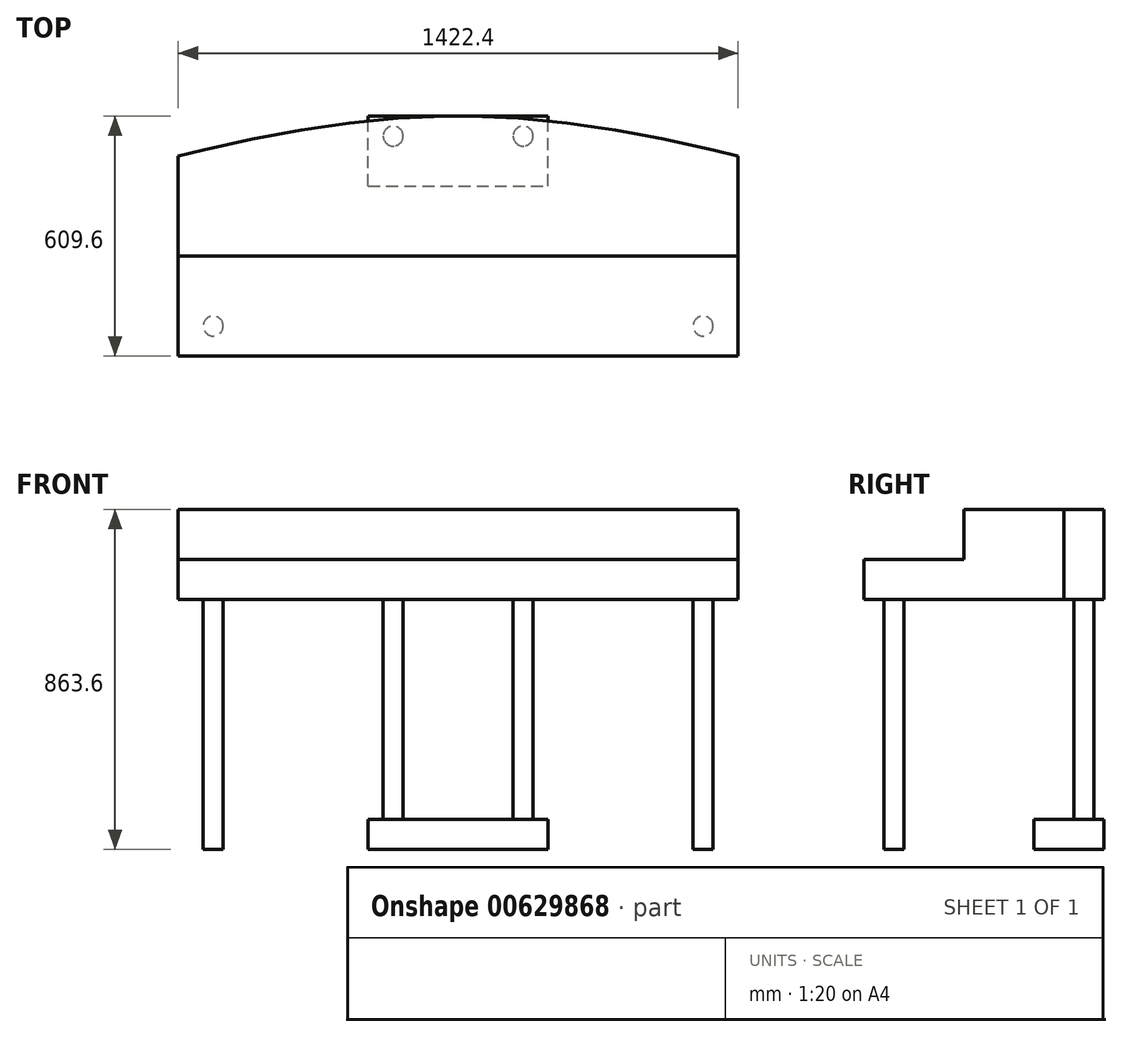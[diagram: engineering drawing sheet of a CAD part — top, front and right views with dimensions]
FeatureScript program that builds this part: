
annotation { "Feature Type Name" : "Feature", "Feature Type Description" : "" }
export const myFeature = defineFeature(function(context is Context, id is Id, definition is map)
    precondition{}
    {
        {
            var Q0;
            Q0=qCreatedBy(makeId("Top.planeOp"),FACE);
            var sketch = newSketch(context, id + "F0", { "sketchPlane" : qUnion([Q0])});
            skLineSegment(sketch, "E0.bottom", {"start": v(0, 0) * mm, "end": v(1422.4, 0) * mm});
            skLineSegment(sketch, "E0.left", {"start": v(0, 0) * mm, "end": v(0, 508) * mm});
            skLineSegment(sketch, "E0.right", {"start": v(1422.4, 0) * mm, "end": v(1422.4, 508) * mm});
            skFitSpline(sketch, "E1", {"points": [v(0, 508) * mm, v(711.2, 609.6) * mm, v(1422.4, 508) * mm], "startDerivative": vector(1449.3, 359.1) * mm, "endDerivative": vector(1449.3, -359.1) * mm});
            skLineSegment(sketch, "E2", {"start": v(711.2, 0) * mm, "end": v(711.2, 609.6) * mm, "construction": true});
            skLineSegment(sketch, "E3", {"start": v(0, 254) * mm, "end": v(1422.4, 254) * mm});
            skCircle(sketch, "E4", {"center": v(546.1, 558.8) * mm, "radius": 25.4 * mm});
            skCircle(sketch, "E5", {"center": v(876.3, 558.8) * mm, "radius": 25.4 * mm});
            skCircle(sketch, "E6", {"center": v(1333.5, 76.2) * mm, "radius": 25.4 * mm});
            skCircle(sketch, "E7", {"center": v(88.9, 76.2) * mm, "radius": 25.4 * mm});
            skSolve(sketch);
        }
        {
            var Q0;
            {var subQ1=sQuery(id+"F0.wireOp",EDGE,"E1");Q0=makeQuery(id+"F0.imprint","IMPRINT",FACE,{"disambiguationData":[TD([[makeQuery(id+"F0.imprint","IMPRINT",EDGE,{"derivedFrom":subQ1}),-1.0]])]});}
            var Q1;
            Q1=makeQuery(id+"F0.imprint","IMPRINT",FACE,{"disambiguationData":[TD([[makeQuery(id+"F0.imprint","IMPRINT",EDGE,{"derivedFrom":sQuery(id+"F0.wireOp",EDGE,"E4")}),1.0]])]});
            var Q2;
            Q2=makeQuery(id+"F0.imprint","IMPRINT",FACE,{"disambiguationData":[TD([[makeQuery(id+"F0.imprint","IMPRINT",EDGE,{"derivedFrom":sQuery(id+"F0.wireOp",EDGE,"E5")}),1.0]])]});
            extrude(context, id + "F1", {"entities" : qUnion([Q0, Q1, Q2]), "depth" : 228.6 * mm, "offsetDistance" : 25.4 * mm});
        }
        {
            var Q0;
            {var subQ1=sQuery(id+"F0.wireOp",EDGE,"E0.bottom");Q0=makeQuery(id+"F0.imprint","IMPRINT",FACE,{"disambiguationData":[TD([[makeQuery(id+"F0.imprint","IMPRINT",EDGE,{"derivedFrom":subQ1}),1.0]])]});}
            var Q1;
            Q1=makeQuery(id+"F0.imprint","IMPRINT",FACE,{"disambiguationData":[TD([[makeQuery(id+"F0.imprint","IMPRINT",EDGE,{"derivedFrom":sQuery(id+"F0.wireOp",EDGE,"E7")}),1.0]])]});
            var Q2;
            Q2=makeQuery(id+"F0.imprint","IMPRINT",FACE,{"disambiguationData":[TD([[makeQuery(id+"F0.imprint","IMPRINT",EDGE,{"derivedFrom":sQuery(id+"F0.wireOp",EDGE,"E6")}),1.0]])]});
            extrude(context, id + "F2", {"entities" : qUnion([Q0, Q1, Q2]), "operationType" : NewBodyOperationType.ADD, "depth" : 101.6 * mm, "offsetDistance" : 25.4 * mm});
        }
        {
            var Q0;
            Q0=makeQuery(id+"F0.imprint","IMPRINT",FACE,{"disambiguationData":[TD([[makeQuery(id+"F0.imprint","IMPRINT",EDGE,{"derivedFrom":sQuery(id+"F0.wireOp",EDGE,"E5")}),1.0]])]});
            var Q1;
            Q1=makeQuery(id+"F0.imprint","IMPRINT",FACE,{"disambiguationData":[TD([[makeQuery(id+"F0.imprint","IMPRINT",EDGE,{"derivedFrom":sQuery(id+"F0.wireOp",EDGE,"E4")}),1.0]])]});
            var Q2;
            Q2=makeQuery(id+"F0.imprint","IMPRINT",FACE,{"disambiguationData":[TD([[makeQuery(id+"F0.imprint","IMPRINT",EDGE,{"derivedFrom":sQuery(id+"F0.wireOp",EDGE,"E6")}),1.0]])]});
            var Q3;
            Q3=makeQuery(id+"F0.imprint","IMPRINT",FACE,{"disambiguationData":[TD([[makeQuery(id+"F0.imprint","IMPRINT",EDGE,{"derivedFrom":sQuery(id+"F0.wireOp",EDGE,"E7")}),1.0]])]});
            var Q4;
            Q4=sQuery(id+"F0.wireOp",EDGE,"E5");
            var Q5;
            Q5=sQuery(id+"F0.wireOp",EDGE,"E4");
            var Q6;
            Q6=sQuery(id+"F0.wireOp",EDGE,"E6");
            var Q7;
            Q7=sQuery(id+"F0.wireOp",EDGE,"E7");
            extrude(context, id + "F3", {"entities" : qUnion([Q0, Q1, Q2, Q3]), "operationType" : NewBodyOperationType.ADD, "surfaceEntities" : qUnion([Q4, Q5, Q6, Q7]), "oppositeDirection" : true, "depth" : 635 * mm, "offsetDistance" : 25.4 * mm});
        }
        {
            var Q0;
            Q0=makeQuery(id+"F3.opExtrude","CAP_FACE",FACE,{"disambiguationData":[OSD([sQuery(id+"F0.wireOp",EDGE,"E4")])],"isStart":false});
            var sketch = newSketch(context, id + "F4", { "sketchPlane" : qUnion([Q0])});
            skLineSegment(sketch, "E8.bottom", {"start": v(482.6, -431.8) * mm, "end": v(939.8, -431.8) * mm});
            skLineSegment(sketch, "E8.top", {"start": v(482.6, -609.6) * mm, "end": v(939.8, -609.6) * mm});
            skLineSegment(sketch, "E8.left", {"start": v(482.6, -431.8) * mm, "end": v(482.6, -609.6) * mm});
            skLineSegment(sketch, "E8.right", {"start": v(939.8, -431.8) * mm, "end": v(939.8, -609.6) * mm});
            skSolve(sketch);
        }
        {
            var Q0;
            Q0 = qSketchRegion(id + "F4", true);
            extrude(context, id + "F5", {"entities" : qUnion([Q0]), "operationType" : NewBodyOperationType.ADD, "oppositeDirection" : true, "depth" : 76.2 * mm, "offsetDistance" : 25.4 * mm});
        }
    });
